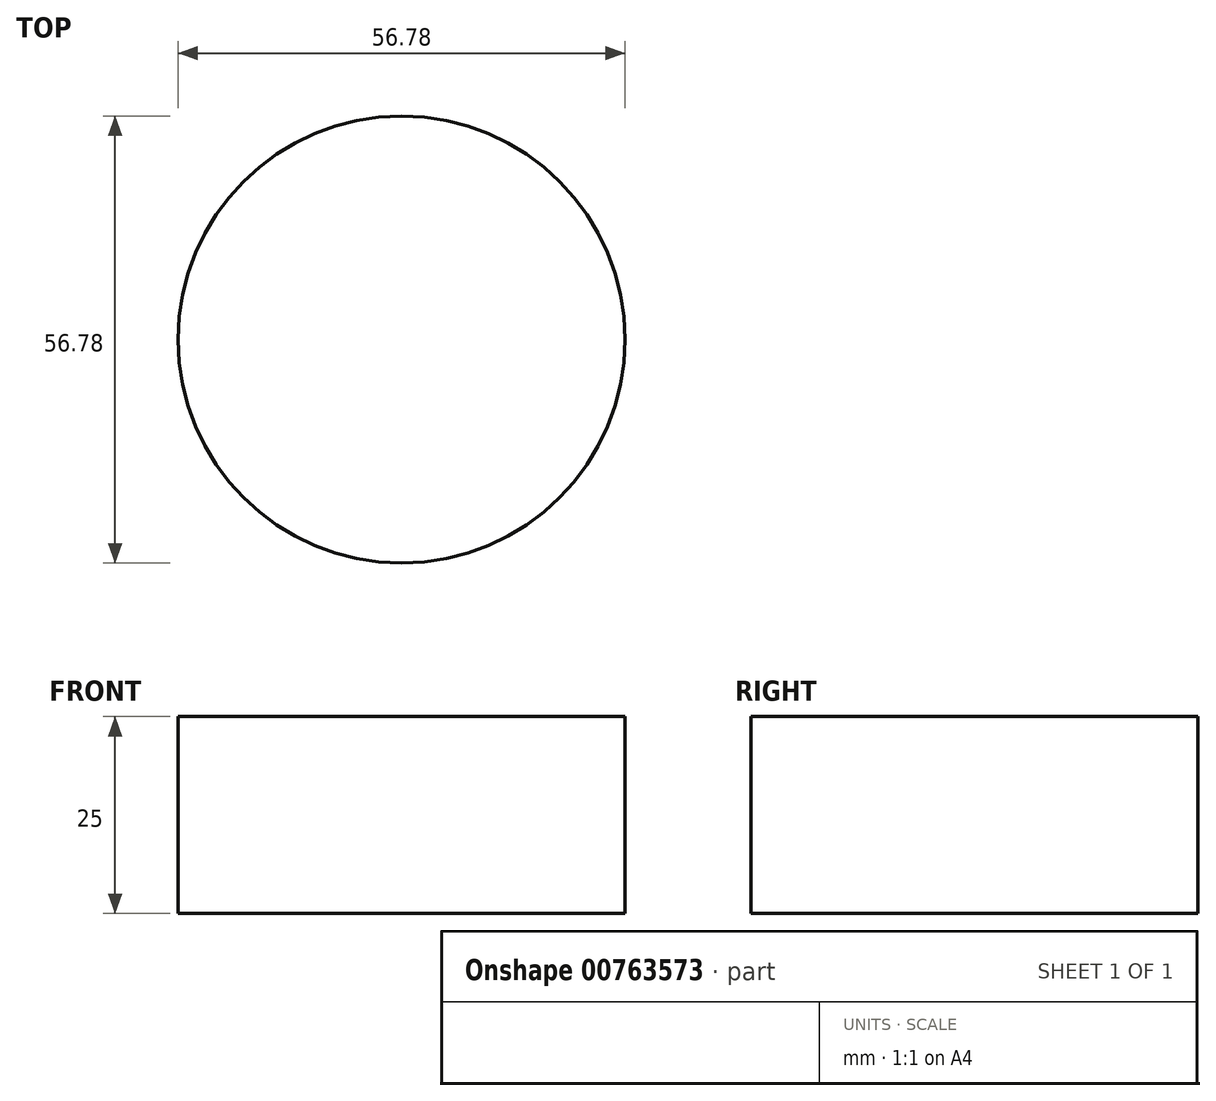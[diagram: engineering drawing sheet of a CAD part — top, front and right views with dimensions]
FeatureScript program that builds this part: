
annotation { "Feature Type Name" : "Feature", "Feature Type Description" : "" }
export const myFeature = defineFeature(function(context is Context, id is Id, definition is map)
    precondition{}
    {
        {
            var Q0;
            Q0=qCreatedBy(makeId("Top.planeOp"),FACE);
            var sketch = newSketch(context, id + "F0", { "sketchPlane" : qUnion([Q0])});
            skCircle(sketch, "E0", {"center": v(0, 0) * mm, "radius": 28.4 * mm});
            skSolve(sketch);
        }
        {
            var Q0;
            Q0=makeQuery(id+"F0.imprint","IMPRINT",FACE,{"disambiguationData":[TD([[makeQuery(id+"F0.imprint","IMPRINT",EDGE,{"derivedFrom":sQuery(id+"F0.wireOp",EDGE,"E0")}),1.0]])]});
            extrude(context, id + "F1", {"entities" : qUnion([Q0]), "depth" : 25 * mm, "offsetDistance" : 25 * mm});
        }
    });
